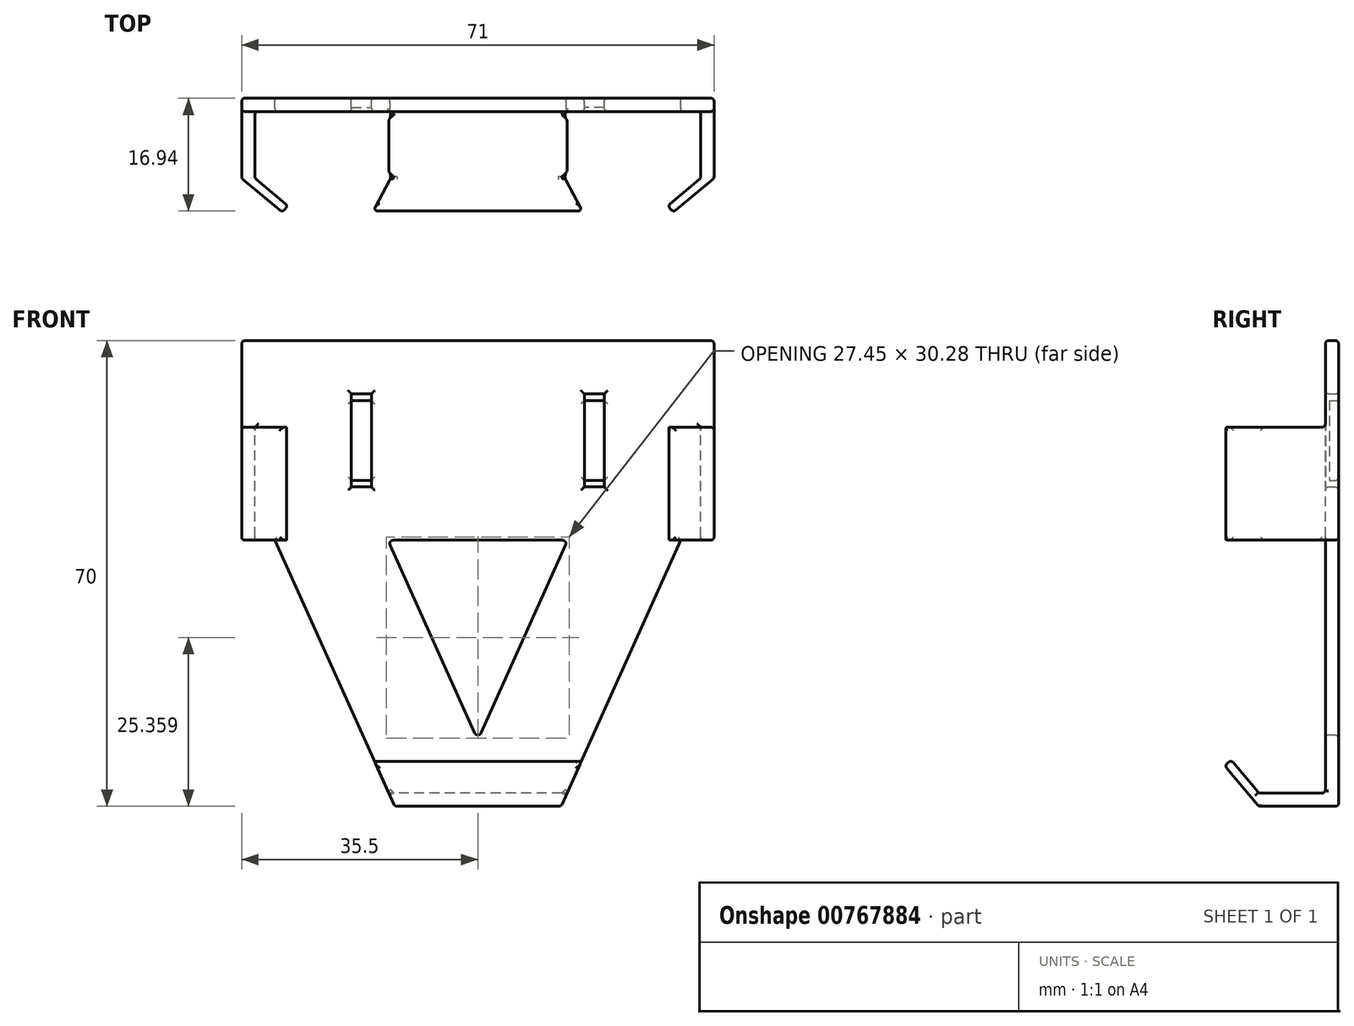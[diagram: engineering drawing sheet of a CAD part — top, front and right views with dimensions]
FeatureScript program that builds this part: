
annotation { "Feature Type Name" : "Feature", "Feature Type Description" : "" }
export const myFeature = defineFeature(function(context is Context, id is Id, definition is map)
    precondition{}
    {
        {
            var Q0;
            Q0=qCreatedBy(makeId("Front.planeOp"),FACE);
            var sketch = newSketch(context, id + "F0", { "sketchPlane" : qUnion([Q0])});
            skLineSegment(sketch, "E0", {"start": v(-12.5, -35) * mm, "end": v(12.5, -35) * mm});
            skLineSegment(sketch, "E1", {"start": v(35.5, 5) * mm, "end": v(35.5, 35) * mm});
            skLineSegment(sketch, "E2", {"start": v(35.5, 35) * mm, "end": v(-35.5, 35) * mm});
            skLineSegment(sketch, "E3", {"start": v(-35.5, 35) * mm, "end": v(-35.5, 5) * mm});
            skLineSegment(sketch, "E4", {"start": v(0, 35) * mm, "end": v(0, -35) * mm, "construction": true});
            skLineSegment(sketch, "E5", {"start": v(35.5, 5) * mm, "end": v(30.5, 5) * mm});
            skLineSegment(sketch, "E6", {"start": v(30.5, 5) * mm, "end": v(12.5, -35) * mm});
            skLineSegment(sketch, "E7", {"start": v(-35.5, 5) * mm, "end": v(-30.5, 5) * mm});
            skLineSegment(sketch, "E8", {"start": v(-30.5, 5) * mm, "end": v(-12.5, -35) * mm});
            skLineSegment(sketch, "E9.bottom", {"start": v(-19, 27) * mm, "end": v(-16, 27) * mm});
            skLineSegment(sketch, "E9.top", {"start": v(-19, 26) * mm, "end": v(-16, 26) * mm});
            skLineSegment(sketch, "E9.left", {"start": v(-19, 27) * mm, "end": v(-19, 26) * mm});
            skLineSegment(sketch, "E9.right", {"start": v(-16, 27) * mm, "end": v(-16, 26) * mm});
            skLineSegment(sketch, "E10.bottom", {"start": v(-19, 14) * mm, "end": v(-16, 14) * mm});
            skLineSegment(sketch, "E10.top", {"start": v(-19, 13) * mm, "end": v(-16, 13) * mm});
            skLineSegment(sketch, "E10.left", {"start": v(-19, 14) * mm, "end": v(-19, 13) * mm});
            skLineSegment(sketch, "E10.right", {"start": v(-16, 14) * mm, "end": v(-16, 13) * mm});
            skLineSegment(sketch, "E11.MirrorCS", {"start": v(16, 14) * mm, "end": v(16, 13) * mm});
            skLineSegment(sketch, "E12.MirrorCS", {"start": v(16, 27) * mm, "end": v(16, 26) * mm});
            skLineSegment(sketch, "E13.MirrorCS", {"start": v(19, 27) * mm, "end": v(19, 26) * mm});
            skLineSegment(sketch, "E14.MirrorCS", {"start": v(19, 14) * mm, "end": v(19, 13) * mm});
            skLineSegment(sketch, "E15.MirrorCS", {"start": v(19, 26) * mm, "end": v(16, 26) * mm});
            skLineSegment(sketch, "E16.MirrorCS", {"start": v(19, 13) * mm, "end": v(16, 13) * mm});
            skLineSegment(sketch, "E17.MirrorCS", {"start": v(19, 14) * mm, "end": v(16, 14) * mm});
            skLineSegment(sketch, "E18.MirrorCS", {"start": v(19, 27) * mm, "end": v(16, 27) * mm});
            skLineSegment(sketch, "E19", {"start": v(0, -25) * mm, "end": v(-13.5, 5) * mm});
            skLineSegment(sketch, "E20", {"start": v(-13.5, 5) * mm, "end": v(13.5, 5) * mm});
            skLineSegment(sketch, "E21", {"start": v(13.5, 5) * mm, "end": v(0, -25) * mm});
            skSolve(sketch);
        }
        {
            var Q0;
            Q0 = qSketchRegion(id + "F0", true);
            extrude(context, id + "F1", {"entities" : qUnion([Q0]), "depth" : 2 * mm, "offsetDistance" : 25 * mm});
        }
        {
            var Q0;
            Q0=makeQuery(id+"F1.opExtrude","CAP_FACE",FACE,{"disambiguationData":[OSD([sQuery(id+"F0.wireOp",EDGE,"E0"),sQuery(id+"F0.wireOp",EDGE,"E1"),sQuery(id+"F0.wireOp",EDGE,"E2"),sQuery(id+"F0.wireOp",EDGE,"E3"),sQuery(id+"F0.wireOp",EDGE,"E5"),sQuery(id+"F0.wireOp",EDGE,"E6"),sQuery(id+"F0.wireOp",EDGE,"E7"),sQuery(id+"F0.wireOp",EDGE,"E8"),sQuery(id+"F0.wireOp",EDGE,"E9.bottom"),sQuery(id+"F0.wireOp",EDGE,"E9.top"),sQuery(id+"F0.wireOp",EDGE,"E9.left"),sQuery(id+"F0.wireOp",EDGE,"E9.right"),sQuery(id+"F0.wireOp",EDGE,"E10.bottom"),sQuery(id+"F0.wireOp",EDGE,"E10.top"),sQuery(id+"F0.wireOp",EDGE,"E10.left"),sQuery(id+"F0.wireOp",EDGE,"E10.right"),sQuery(id+"F0.wireOp",EDGE,"E11.MirrorCS"),sQuery(id+"F0.wireOp",EDGE,"E12.MirrorCS"),sQuery(id+"F0.wireOp",EDGE,"E13.MirrorCS"),sQuery(id+"F0.wireOp",EDGE,"E14.MirrorCS"),sQuery(id+"F0.wireOp",EDGE,"E15.MirrorCS"),sQuery(id+"F0.wireOp",EDGE,"E16.MirrorCS"),sQuery(id+"F0.wireOp",EDGE,"E17.MirrorCS"),sQuery(id+"F0.wireOp",EDGE,"E18.MirrorCS"),sQuery(id+"F0.wireOp",EDGE,"E19"),sQuery(id+"F0.wireOp",EDGE,"E20"),sQuery(id+"F0.wireOp",EDGE,"E21")])],"isStart":false});
            var sketch = newSketch(context, id + "F2", { "sketchPlane" : qUnion([Q0])});
            skLineSegment(sketch, "E22.bottom", {"start": v(-19, 26) * mm, "end": v(-16, 26) * mm});
            skLineSegment(sketch, "E22.top", {"start": v(-19, 14) * mm, "end": v(-16, 14) * mm});
            skLineSegment(sketch, "E22.left", {"start": v(-19, 26) * mm, "end": v(-19, 14) * mm});
            skLineSegment(sketch, "E22.right", {"start": v(-16, 26) * mm, "end": v(-16, 14) * mm});
            skLineSegment(sketch, "E23.bottom", {"start": v(16, 26) * mm, "end": v(19, 26) * mm});
            skLineSegment(sketch, "E23.top", {"start": v(16, 14) * mm, "end": v(19, 14) * mm});
            skLineSegment(sketch, "E23.left", {"start": v(16, 26) * mm, "end": v(16, 14) * mm});
            skLineSegment(sketch, "E23.right", {"start": v(19, 26) * mm, "end": v(19, 14) * mm});
            skSolve(sketch);
        }
        {
            var Q0;
            Q0 = qSketchRegion(id + "F2", true);
            extrude(context, id + "F3", {"entities" : qUnion([Q0]), "operationType" : NewBodyOperationType.REMOVE, "oppositeDirection" : true, "depth" : 0.6 * mm, "offsetDistance" : 25 * mm});
        }
        {
            var Q0;
            Q0=makeQuery(id+"F1.opExtrude","CAP_FACE",FACE,{"disambiguationData":[OSD([sQuery(id+"F0.wireOp",EDGE,"E0"),sQuery(id+"F0.wireOp",EDGE,"E1"),sQuery(id+"F0.wireOp",EDGE,"E2"),sQuery(id+"F0.wireOp",EDGE,"E3"),sQuery(id+"F0.wireOp",EDGE,"E5"),sQuery(id+"F0.wireOp",EDGE,"E6"),sQuery(id+"F0.wireOp",EDGE,"E7"),sQuery(id+"F0.wireOp",EDGE,"E8"),sQuery(id+"F0.wireOp",EDGE,"E9.bottom"),sQuery(id+"F0.wireOp",EDGE,"E9.top"),sQuery(id+"F0.wireOp",EDGE,"E9.left"),sQuery(id+"F0.wireOp",EDGE,"E9.right"),sQuery(id+"F0.wireOp",EDGE,"E10.bottom"),sQuery(id+"F0.wireOp",EDGE,"E10.top"),sQuery(id+"F0.wireOp",EDGE,"E10.left"),sQuery(id+"F0.wireOp",EDGE,"E10.right"),sQuery(id+"F0.wireOp",EDGE,"E11.MirrorCS"),sQuery(id+"F0.wireOp",EDGE,"E12.MirrorCS"),sQuery(id+"F0.wireOp",EDGE,"E13.MirrorCS"),sQuery(id+"F0.wireOp",EDGE,"E14.MirrorCS"),sQuery(id+"F0.wireOp",EDGE,"E15.MirrorCS"),sQuery(id+"F0.wireOp",EDGE,"E16.MirrorCS"),sQuery(id+"F0.wireOp",EDGE,"E17.MirrorCS"),sQuery(id+"F0.wireOp",EDGE,"E18.MirrorCS"),sQuery(id+"F0.wireOp",EDGE,"E19"),sQuery(id+"F0.wireOp",EDGE,"E20"),sQuery(id+"F0.wireOp",EDGE,"E21")])],"isStart":false});
            var sketch = newSketch(context, id + "F4", { "sketchPlane" : qUnion([Q0])});
            skLineSegment(sketch, "E24.bottom", {"start": v(-35.5, 5) * mm, "end": v(-33.5, 5) * mm});
            skLineSegment(sketch, "E24.top", {"start": v(-35.5, 22) * mm, "end": v(-33.5, 22) * mm});
            skLineSegment(sketch, "E24.left", {"start": v(-35.5, 5) * mm, "end": v(-35.5, 22) * mm});
            skLineSegment(sketch, "E24.right", {"start": v(-33.5, 5) * mm, "end": v(-33.5, 22) * mm});
            skLineSegment(sketch, "E25.bottom", {"start": v(35.5, 5) * mm, "end": v(33.5, 5) * mm});
            skLineSegment(sketch, "E25.top", {"start": v(35.5, 22) * mm, "end": v(33.5, 22) * mm});
            skLineSegment(sketch, "E25.left", {"start": v(35.5, 5) * mm, "end": v(35.5, 22) * mm});
            skLineSegment(sketch, "E25.right", {"start": v(33.5, 5) * mm, "end": v(33.5, 22) * mm});
            skLineSegment(sketch, "E26", {"start": v(-12.5, -35) * mm, "end": v(12.5, -35) * mm});
            skLineSegment(sketch, "E27", {"start": v(12.5, -35) * mm, "end": v(13.4, -33) * mm});
            skLineSegment(sketch, "E28", {"start": v(13.4, -33) * mm, "end": v(-13.4, -33) * mm});
            skLineSegment(sketch, "E29", {"start": v(-13.4, -33) * mm, "end": v(-12.5, -35) * mm});
            skSolve(sketch);
        }
        {
            var Q0;
            Q0 = qSketchRegion(id + "F4", true);
            extrude(context, id + "F5", {"entities" : qUnion([Q0]), "operationType" : NewBodyOperationType.ADD, "depth" : 10 * mm, "offsetDistance" : 25 * mm});
        }
        {
            var Q0;
            Q0=makeQuery(id+"F5.boolean.opBoolean","MERGE",FACE,{"derivedFrom":[makeQuery(id+"F1.opExtrude","SWEPT_FACE",FACE,{"disambiguationData":[OSD([sQuery(id+"F0.wireOp",EDGE,"E7")])]}),makeQuery(id+"F5.opExtrude","SWEPT_FACE",FACE,{"disambiguationData":[OSD([sQuery(id+"F4.wireOp",EDGE,"E24.bottom")])]})]});
            var sketch = newSketch(context, id + "F6", { "sketchPlane" : qUnion([Q0])});
            skLineSegment(sketch, "E30", {"start": v(-35.5, 12) * mm, "end": v(-29.37, 17.14) * mm});
            skLineSegment(sketch, "E31", {"start": v(-29.37, 17.14) * mm, "end": v(-28.55, 16.16) * mm});
            skLineSegment(sketch, "E32", {"start": v(-28.55, 16.16) * mm, "end": v(-33.5, 12) * mm});
            skLineSegment(sketch, "E33", {"start": v(-33.5, 12) * mm, "end": v(-35.5, 12) * mm});
            skLineSegment(sketch, "E34", {"start": v(0, 0) * mm, "end": v(0, 20.41) * mm, "construction": true});
            skLineSegment(sketch, "E35.MirrorCS", {"start": v(29.37, 17.14) * mm, "end": v(28.55, 16.16) * mm});
            skLineSegment(sketch, "E36.MirrorCS", {"start": v(33.5, 12) * mm, "end": v(35.5, 12) * mm});
            skLineSegment(sketch, "E37.MirrorCS", {"start": v(28.55, 16.16) * mm, "end": v(33.5, 12) * mm});
            skLineSegment(sketch, "E38.MirrorCS", {"start": v(35.5, 12) * mm, "end": v(29.37, 17.14) * mm});
            skSolve(sketch);
        }
        {
            var Q0;
            Q0 = qSketchRegion(id + "F6", true);
            var Q1;
            Q1=makeQuery(id+"F5.opExtrude","SWEPT_FACE",FACE,{"disambiguationData":[OSD([sQuery(id+"F4.wireOp",EDGE,"E24.top")])]});
            extrude(context, id + "F7", {"entities" : qUnion([Q0]), "operationType" : NewBodyOperationType.ADD, "endBound" : BoundingType.UP_TO_SURFACE, "oppositeDirection" : true, "depth" : 15 * mm, "endBoundEntityFace" : qUnion([Q1]), "offsetDistance" : 25 * mm});
        }
        {
            var Q0;
            Q0=qCreatedBy(makeId("Right.planeOp"),FACE);
            var sketch = newSketch(context, id + "F8", { "sketchPlane" : qUnion([Q0])});
            skLineSegment(sketch, "E39", {"start": v(-12, -33) * mm, "end": v(-16.16, -28.05) * mm});
            skLineSegment(sketch, "E40", {"start": v(-16.16, -28.05) * mm, "end": v(-17.14, -28.87) * mm});
            skLineSegment(sketch, "E41", {"start": v(-17.14, -28.87) * mm, "end": v(-12, -35) * mm});
            skLineSegment(sketch, "E42", {"start": v(-12, -35) * mm, "end": v(-12, -33) * mm});
            skSolve(sketch);
        }
        {
            var Q0;
            Q0 = qSketchRegion(id + "F8", true);
            extrude(context, id + "F9", {"entities" : qUnion([Q0]), "operationType" : NewBodyOperationType.ADD, "endBound" : BoundingType.SYMMETRIC, "depth" : 35 * mm, "offsetDistance" : 25 * mm});
        }
        {
            var Q0;
            Q0=makeQuery(id+"F1.opExtrude","CAP_FACE",FACE,{"disambiguationData":[OSD([sQuery(id+"F0.wireOp",EDGE,"E0"),sQuery(id+"F0.wireOp",EDGE,"E1"),sQuery(id+"F0.wireOp",EDGE,"E2"),sQuery(id+"F0.wireOp",EDGE,"E3"),sQuery(id+"F0.wireOp",EDGE,"E5"),sQuery(id+"F0.wireOp",EDGE,"E6"),sQuery(id+"F0.wireOp",EDGE,"E7"),sQuery(id+"F0.wireOp",EDGE,"E8"),sQuery(id+"F0.wireOp",EDGE,"E9.bottom"),sQuery(id+"F0.wireOp",EDGE,"E9.top"),sQuery(id+"F0.wireOp",EDGE,"E9.left"),sQuery(id+"F0.wireOp",EDGE,"E9.right"),sQuery(id+"F0.wireOp",EDGE,"E10.bottom"),sQuery(id+"F0.wireOp",EDGE,"E10.top"),sQuery(id+"F0.wireOp",EDGE,"E10.left"),sQuery(id+"F0.wireOp",EDGE,"E10.right"),sQuery(id+"F0.wireOp",EDGE,"E11.MirrorCS"),sQuery(id+"F0.wireOp",EDGE,"E12.MirrorCS"),sQuery(id+"F0.wireOp",EDGE,"E13.MirrorCS"),sQuery(id+"F0.wireOp",EDGE,"E14.MirrorCS"),sQuery(id+"F0.wireOp",EDGE,"E15.MirrorCS"),sQuery(id+"F0.wireOp",EDGE,"E16.MirrorCS"),sQuery(id+"F0.wireOp",EDGE,"E17.MirrorCS"),sQuery(id+"F0.wireOp",EDGE,"E18.MirrorCS"),sQuery(id+"F0.wireOp",EDGE,"E19"),sQuery(id+"F0.wireOp",EDGE,"E20"),sQuery(id+"F0.wireOp",EDGE,"E21")])],"isStart":true});
            var sketch = newSketch(context, id + "F10", { "sketchPlane" : qUnion([Q0])});
            skLineSegment(sketch, "E43", {"start": v(12.5, -35) * mm, "end": v(15.63, -28.05) * mm});
            skLineSegment(sketch, "E44", {"start": v(15.63, -28.05) * mm, "end": v(17.5, -28.05) * mm});
            skLineSegment(sketch, "E45", {"start": v(17.5, -28.05) * mm, "end": v(17.5, -35) * mm});
            skLineSegment(sketch, "E46", {"start": v(17.5, -35) * mm, "end": v(12.5, -35) * mm});
            skLineSegment(sketch, "E47.MirrorCS", {"start": v(-15.63, -28.05) * mm, "end": v(-17.5, -28.05) * mm});
            skLineSegment(sketch, "E48.MirrorCS", {"start": v(-12.5, -35) * mm, "end": v(-15.63, -28.05) * mm});
            skLineSegment(sketch, "E49.MirrorCS", {"start": v(-17.5, -35) * mm, "end": v(-12.5, -35) * mm});
            skLineSegment(sketch, "E50.MirrorCS", {"start": v(-17.5, -28.05) * mm, "end": v(-17.5, -35) * mm});
            skSolve(sketch);
        }
        {
            var Q0;
            Q0 = qSketchRegion(id + "F10", true);
            extrude(context, id + "F11", {"entities" : qUnion([Q0]), "operationType" : NewBodyOperationType.REMOVE, "endBound" : BoundingType.THROUGH_ALL, "oppositeDirection" : true, "depth" : 25 * mm, "offsetDistance" : 25 * mm});
        }
        {
            var Q0;
            Q0=makeQuery(id+"F1.opExtrude","CAP_FACE",FACE,{"disambiguationData":[OSD([sQuery(id+"F0.wireOp",EDGE,"E0"),sQuery(id+"F0.wireOp",EDGE,"E1"),sQuery(id+"F0.wireOp",EDGE,"E2"),sQuery(id+"F0.wireOp",EDGE,"E3"),sQuery(id+"F0.wireOp",EDGE,"E5"),sQuery(id+"F0.wireOp",EDGE,"E6"),sQuery(id+"F0.wireOp",EDGE,"E7"),sQuery(id+"F0.wireOp",EDGE,"E8"),sQuery(id+"F0.wireOp",EDGE,"E9.bottom"),sQuery(id+"F0.wireOp",EDGE,"E9.top"),sQuery(id+"F0.wireOp",EDGE,"E9.left"),sQuery(id+"F0.wireOp",EDGE,"E9.right"),sQuery(id+"F0.wireOp",EDGE,"E10.bottom"),sQuery(id+"F0.wireOp",EDGE,"E10.top"),sQuery(id+"F0.wireOp",EDGE,"E10.left"),sQuery(id+"F0.wireOp",EDGE,"E10.right"),sQuery(id+"F0.wireOp",EDGE,"E11.MirrorCS"),sQuery(id+"F0.wireOp",EDGE,"E12.MirrorCS"),sQuery(id+"F0.wireOp",EDGE,"E13.MirrorCS"),sQuery(id+"F0.wireOp",EDGE,"E14.MirrorCS"),sQuery(id+"F0.wireOp",EDGE,"E15.MirrorCS"),sQuery(id+"F0.wireOp",EDGE,"E16.MirrorCS"),sQuery(id+"F0.wireOp",EDGE,"E17.MirrorCS"),sQuery(id+"F0.wireOp",EDGE,"E18.MirrorCS"),sQuery(id+"F0.wireOp",EDGE,"E19"),sQuery(id+"F0.wireOp",EDGE,"E20"),sQuery(id+"F0.wireOp",EDGE,"E21")])],"isStart":true});
            var Q1;
            Q1=makeQuery(id+"F1.opExtrude","CAP_FACE",FACE,{"disambiguationData":[OSD([sQuery(id+"F0.wireOp",EDGE,"E0"),sQuery(id+"F0.wireOp",EDGE,"E1"),sQuery(id+"F0.wireOp",EDGE,"E2"),sQuery(id+"F0.wireOp",EDGE,"E3"),sQuery(id+"F0.wireOp",EDGE,"E5"),sQuery(id+"F0.wireOp",EDGE,"E6"),sQuery(id+"F0.wireOp",EDGE,"E7"),sQuery(id+"F0.wireOp",EDGE,"E8"),sQuery(id+"F0.wireOp",EDGE,"E9.bottom"),sQuery(id+"F0.wireOp",EDGE,"E9.top"),sQuery(id+"F0.wireOp",EDGE,"E9.left"),sQuery(id+"F0.wireOp",EDGE,"E9.right"),sQuery(id+"F0.wireOp",EDGE,"E10.bottom"),sQuery(id+"F0.wireOp",EDGE,"E10.top"),sQuery(id+"F0.wireOp",EDGE,"E10.left"),sQuery(id+"F0.wireOp",EDGE,"E10.right"),sQuery(id+"F0.wireOp",EDGE,"E11.MirrorCS"),sQuery(id+"F0.wireOp",EDGE,"E12.MirrorCS"),sQuery(id+"F0.wireOp",EDGE,"E13.MirrorCS"),sQuery(id+"F0.wireOp",EDGE,"E14.MirrorCS"),sQuery(id+"F0.wireOp",EDGE,"E15.MirrorCS"),sQuery(id+"F0.wireOp",EDGE,"E16.MirrorCS"),sQuery(id+"F0.wireOp",EDGE,"E17.MirrorCS"),sQuery(id+"F0.wireOp",EDGE,"E18.MirrorCS"),sQuery(id+"F0.wireOp",EDGE,"E19"),sQuery(id+"F0.wireOp",EDGE,"E20"),sQuery(id+"F0.wireOp",EDGE,"E21")])],"isStart":false});
            var Q2;
            Q2=makeQuery(id+"F7.opExtrude","SWEPT_FACE",FACE,{"disambiguationData":[OSD([sQuery(id+"F6.wireOp",EDGE,"E32")])]});
            var Q3;
            Q3=makeQuery(id+"F5.boolean.opBoolean","MERGE",FACE,{"derivedFrom":[makeQuery(id+"F1.opExtrude","SWEPT_FACE",FACE,{"disambiguationData":[OSD([sQuery(id+"F0.wireOp",EDGE,"E3")])]}),makeQuery(id+"F5.opExtrude","SWEPT_FACE",FACE,{"disambiguationData":[OSD([sQuery(id+"F4.wireOp",EDGE,"E24.left")])]})]});
            var Q4;
            Q4=makeQuery(id+"F7.opExtrude","SWEPT_FACE",FACE,{"disambiguationData":[OSD([sQuery(id+"F6.wireOp",EDGE,"E30")])]});
            var Q5;
            Q5=makeQuery(id+"F9.opExtrude","SWEPT_FACE",FACE,{"disambiguationData":[OSD([sQuery(id+"F8.wireOp",EDGE,"E39")])]});
            var Q6;
            Q6=makeQuery(id+"F5.boolean.opBoolean","MERGE",FACE,{"derivedFrom":[makeQuery(id+"F1.opExtrude","SWEPT_FACE",FACE,{"disambiguationData":[OSD([sQuery(id+"F0.wireOp",EDGE,"E0")])]}),makeQuery(id+"F5.opExtrude","SWEPT_FACE",FACE,{"disambiguationData":[OSD([sQuery(id+"F4.wireOp",EDGE,"E26")])]})]});
            var Q7;
            Q7=makeQuery(id+"F9.opExtrude","SWEPT_FACE",FACE,{"disambiguationData":[OSD([sQuery(id+"F8.wireOp",EDGE,"E41")])]});
            var Q8;
            Q8=makeQuery(id+"F5.boolean.opBoolean","MERGE",FACE,{"derivedFrom":[makeQuery(id+"F1.opExtrude","SWEPT_FACE",FACE,{"disambiguationData":[OSD([sQuery(id+"F0.wireOp",EDGE,"E1")])]}),makeQuery(id+"F5.opExtrude","SWEPT_FACE",FACE,{"disambiguationData":[OSD([sQuery(id+"F4.wireOp",EDGE,"E25.left")])]})]});
            var Q9;
            Q9=makeQuery(id+"F7.opExtrude","SWEPT_FACE",FACE,{"disambiguationData":[OSD([sQuery(id+"F6.wireOp",EDGE,"E38.MirrorCS")])]});
            var Q10;
            Q10=makeQuery(id+"F7.opExtrude","SWEPT_FACE",FACE,{"disambiguationData":[OSD([sQuery(id+"F6.wireOp",EDGE,"E37.MirrorCS")])]});
            var Q11;
            Q11=makeQuery(id+"F3.boolean.opBoolean","COPY",EDGE,{"derivedFrom":makeQuery(id+"F3.opExtrude","CAP_EDGE",EDGE,{"disambiguationData":[OSD([sQuery(id+"F2.wireOp",EDGE,"E23.top")])],"isStart":false})});
            var Q12;
            Q12=makeQuery(id+"F3.boolean.opBoolean","COPY",EDGE,{"derivedFrom":makeQuery(id+"F3.opExtrude","CAP_EDGE",EDGE,{"disambiguationData":[OSD([sQuery(id+"F2.wireOp",EDGE,"E23.bottom")])],"isStart":false})});
            var Q13;
            Q13=makeQuery(id+"F3.boolean.opBoolean","COPY",EDGE,{"derivedFrom":makeQuery(id+"F3.opExtrude","CAP_EDGE",EDGE,{"disambiguationData":[OSD([sQuery(id+"F2.wireOp",EDGE,"E22.bottom")])],"isStart":false})});
            var Q14;
            Q14=makeQuery(id+"F3.boolean.opBoolean","COPY",EDGE,{"derivedFrom":makeQuery(id+"F3.opExtrude","CAP_EDGE",EDGE,{"disambiguationData":[OSD([sQuery(id+"F2.wireOp",EDGE,"E22.top")])],"isStart":false})});
            var Q15;
            Q15=makeQuery(id+"F1.opExtrude","SWEPT_EDGE",EDGE,{"disambiguationData":[OSD([sQuery(id+"F0.wireOp",EDGE,"E19"),sQuery(id+"F0.wireOp",EDGE,"E20")])]});
            var Q16;
            Q16=makeQuery(id+"F1.opExtrude","SWEPT_EDGE",EDGE,{"disambiguationData":[OSD([sQuery(id+"F0.wireOp",EDGE,"E20"),sQuery(id+"F0.wireOp",EDGE,"E21")])]});
            var Q17;
            Q17=makeQuery(id+"F1.opExtrude","SWEPT_EDGE",EDGE,{"disambiguationData":[OSD([sQuery(id+"F0.wireOp",EDGE,"E19"),sQuery(id+"F0.wireOp",EDGE,"E21")])]});
            fillet(context, id + "F12", {"entities" : qUnion([Q0, Q1, Q2, Q3, Q4, Q5, Q6, Q7, Q8, Q9, Q10, Q11, Q12, Q13, Q14, Q15, Q16, Q17]), "radius" : .5 * mm, "tangentPropagation" : true, "allowEdgeOverflow" : false});
        }
    });
